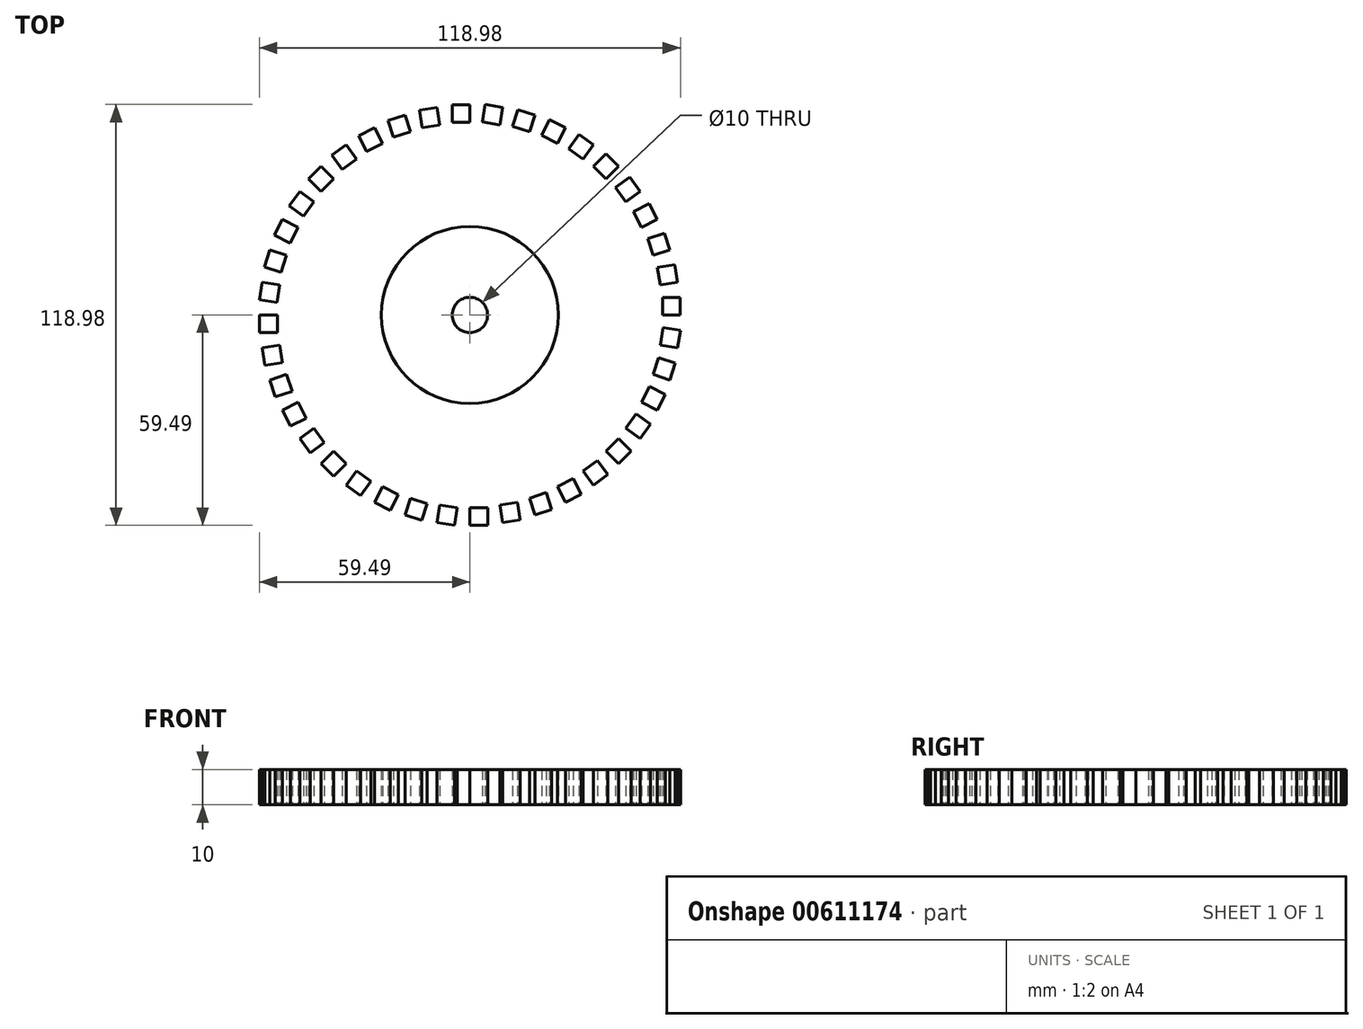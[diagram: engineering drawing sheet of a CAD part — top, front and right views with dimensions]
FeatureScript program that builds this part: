
annotation { "Feature Type Name" : "Feature", "Feature Type Description" : "" }
export const myFeature = defineFeature(function(context is Context, id is Id, definition is map)
    precondition{}
    {
        {
            var Q0;
            Q0=qCreatedBy(makeId("Top.planeOp"),FACE);
            var sketch = newSketch(context, id + "F0", { "sketchPlane" : qUnion([Q0])});
            skCircle(sketch, "E0", {"center": v(0, 0) * mm, "radius": 25 * mm});
            skCircle(sketch, "E1", {"center": v(0, 0) * mm, "radius": 5 * mm});
            skSolve(sketch);
        }
        {
            var Q0;
            Q0 = qSketchRegion(id + "F0", true);
            extrude(context, id + "F1", {"entities" : qUnion([Q0]), "depth" : 10 * mm, "offsetDistance" : 25 * mm});
        }
        {
            var Q0;
            Q0=qCreatedBy(makeId("Top.planeOp"),FACE);
            var sketch = newSketch(context, id + "F2", { "sketchPlane" : qUnion([Q0])});
            skLineSegment(sketch, "E2.bottom", {"start": v(54.44, 0) * mm, "end": v(59.44, 0) * mm});
            skLineSegment(sketch, "E2.top", {"start": v(54.44, 5) * mm, "end": v(59.44, 5) * mm});
            skLineSegment(sketch, "E2.left", {"start": v(54.44, 0) * mm, "end": v(54.44, 5) * mm});
            skLineSegment(sketch, "E2.right", {"start": v(59.44, 0) * mm, "end": v(59.44, 5) * mm});
            skSolve(sketch);
        }
        {
            var Q0;
            Q0 = qSketchRegion(id + "F2", true);
            extrude(context, id + "F3", {"entities" : qUnion([Q0]), "depth" : 10 * mm, "offsetDistance" : 25 * mm});
        }
        {
            var Q0;
            Q0=makeQuery(id+"F3.opExtrude","SWEPT_BODY",BODY,{"disambiguationData":[OSD([sQuery(id+"F2.wireOp",EDGE,"E2.bottom"),sQuery(id+"F2.wireOp",EDGE,"E2.top"),sQuery(id+"F2.wireOp",EDGE,"E2.left"),sQuery(id+"F2.wireOp",EDGE,"E2.right")])]});
            var Q1;
            Q1=makeQuery(id+"F1.opExtrude","CAP_EDGE",EDGE,{"disambiguationData":[OSD([sQuery(id+"F0.wireOp",EDGE,"E1")])],"isStart":true});
            circularPattern(context, id + "F4", {"entities" : qUnion([Q0]), "axis" : qUnion([Q1]), "angle" : 360 * degree, "instanceCount" : 40, "equalSpace" : true});
        }
    });
